# Revit family: Difusores abiertos para aplicaciones generales_Aguilera Extincion
name_source: partatom
category: Rociadores
revit_build: Autodesk Revit 2017 (Build: 20160225_1515(x64)
units: mm (PartAtom-declared; Revit-internal decimal feet)

## family parameters
Compartido = No
Corte con vacíos al cargar = No
Cota de conector redondo = Radio de uso
Mantener orientación de anotación = No
Número OmniClass = 23.65.70.17.11.24
Punto de cálculo de habitación = No
Se basa en plano de trabajo = Sí
Siempre vertical = Sí
Tipo de pieza = Normal
Título OmniClass = Fire Fighting Sprinkler Heads

## types (4) — shared parameters
Clase de presión = Norma
Cobertura = Norma
Descripción = Cabeza nebulizadora abierta para instalación en tubería seca, toberas montadas a 90º y 120º a un rango de caudales suficiente para cubrir una amplia gama de riesgos.
Elevación por defecto = 1219 mm
Fabricante = Aguilera Electrónica
Orificio = Norma
Respuesta = Norma
Símbolo = Sí
Símbolo texto modelo = Sí
URL = http://aguilera.es
Zona de acción = Sí

## per-type parameters (varying)
| type | 120 | 90 | Flujo | Flujo máximo | Flujo mínimo | Modelo | Ángulo |
| Difusor abierto 4 toberas 90º - 1,6 a 20,4 l/min | No | Sí | 1.6 L/min | 20.4 L/min | 1.6 L/min | AN/CA90T4 | 133.03° |
| Difusor abierto 5 toberas 120º -  2,0 a 25,5 l/min | Sí | No | 2.0 L/min | 25.5 L/min | 2.0 L/min | AN/CA120T5 | 120.00° |
| Difusor abierto 5 toberas 90º - 2 a 25,5 l/min | No | Sí | 2.0 L/min | 25.5 L/min | 2.0 L/min | AN/CA90T5 | 133.03° |
| Difusor abierto 7 toberas 120º -  2,8 a 35,7 l/min | Sí | No | 2.0 L/min | 25.5 L/min | 2.0 L/min | AN/CA120T7 | 120.00° |
